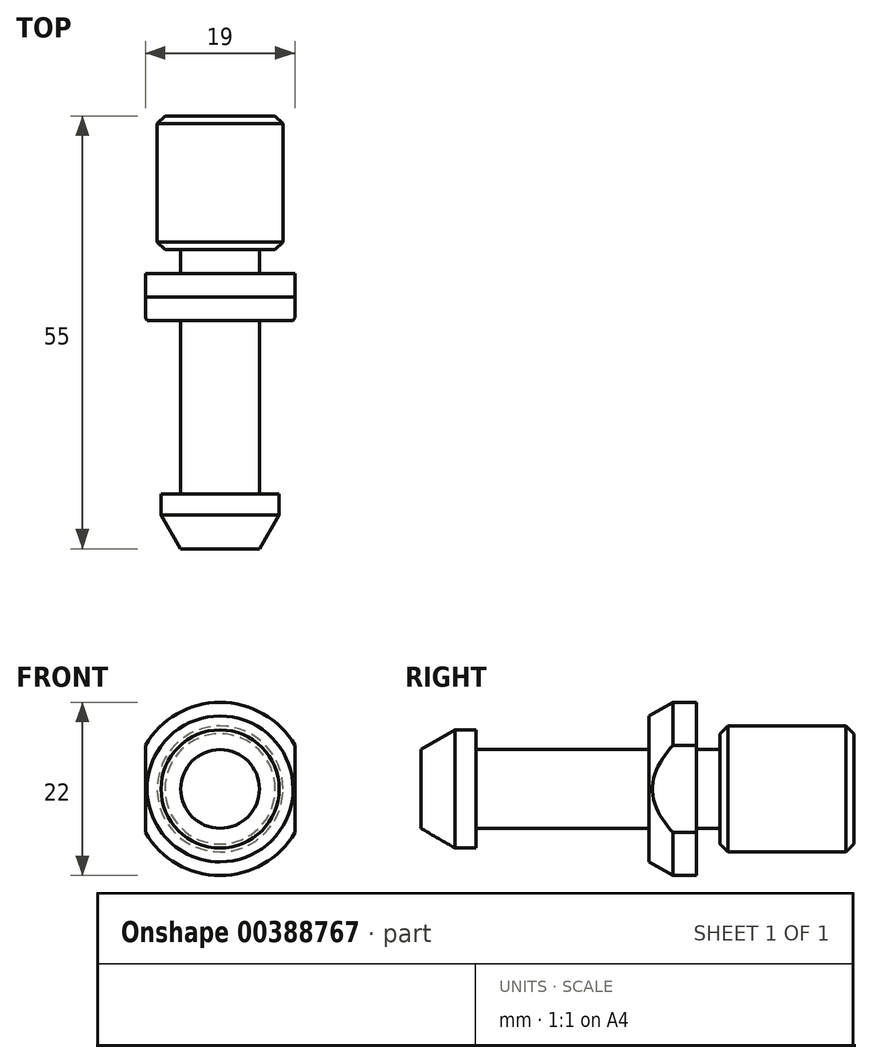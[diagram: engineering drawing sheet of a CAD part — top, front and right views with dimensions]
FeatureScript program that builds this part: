
annotation { "Feature Type Name" : "Feature", "Feature Type Description" : "" }
export const myFeature = defineFeature(function(context is Context, id is Id, definition is map)
    precondition{}
    {
        {
            var Q0;
            Q0=qCreatedBy(makeId("Right.planeOp"),FACE);
            var sketch = newSketch(context, id + "F0", { "sketchPlane" : qUnion([Q0])});
            skLineSegment(sketch, "E0", {"start": v(-37.86, 0) * mm, "end": v(38.7, 0) * mm, "construction": true});
            skLineSegment(sketch, "E1.bottom", {"start": v(0, 0) * mm, "end": v(-22, 0) * mm});
            skLineSegment(sketch, "E1.top", {"start": v(0, 5) * mm, "end": v(-22, 5) * mm});
            skLineSegment(sketch, "E1.left", {"start": v(0, 0) * mm, "end": v(0, 5) * mm});
            skLineSegment(sketch, "E1.right", {"start": v(-22, 0) * mm, "end": v(-22, 5) * mm});
            skLineSegment(sketch, "E2.bottom", {"start": v(-22, 0) * mm, "end": v(-24.67, 0) * mm});
            skLineSegment(sketch, "E2.top", {"start": v(-22, 7.5) * mm, "end": v(-24.67, 7.5) * mm});
            skLineSegment(sketch, "E2.left", {"start": v(-22, 0) * mm, "end": v(-22, 7.5) * mm});
            skLineSegment(sketch, "E2.right", {"start": v(-24.67, 0) * mm, "end": v(-24.67, 7.5) * mm});
            skLineSegment(sketch, "E3", {"start": v(-24.67, 7.5) * mm, "end": v(-29, 5) * mm});
            skLineSegment(sketch, "E4", {"start": v(-29, 5) * mm, "end": v(-29, 0) * mm});
            skLineSegment(sketch, "E5", {"start": v(-29, 5) * mm, "end": v(-22, 5) * mm, "construction": true});
            skLineSegment(sketch, "E6.bottom", {"start": v(0, 0) * mm, "end": v(6, 0) * mm, "construction": true});
            skLineSegment(sketch, "E6.top", {"start": v(0, 11) * mm, "end": v(6, 11) * mm, "construction": true});
            skLineSegment(sketch, "E6.left", {"start": v(0, 0) * mm, "end": v(0, 11) * mm, "construction": true});
            skLineSegment(sketch, "E6.right", {"start": v(6, 0) * mm, "end": v(6, 11) * mm, "construction": true});
            skLineSegment(sketch, "E7.bottom", {"start": v(6, 0) * mm, "end": v(3, 0) * mm});
            skLineSegment(sketch, "E7.top", {"start": v(6, 11) * mm, "end": v(3, 11) * mm});
            skLineSegment(sketch, "E7.left", {"start": v(6, 0) * mm, "end": v(6, 11) * mm});
            skLineSegment(sketch, "E7.right", {"start": v(3, 0) * mm, "end": v(3, 11) * mm});
            skLineSegment(sketch, "E8", {"start": v(3, 11) * mm, "end": v(0, 9.27) * mm});
            skLineSegment(sketch, "E9", {"start": v(0, 9.27) * mm, "end": v(0, 0) * mm});
            skLineSegment(sketch, "E10", {"start": v(0, 0) * mm, "end": v(6, 0) * mm});
            skLineSegment(sketch, "E11", {"start": v(-29, 0) * mm, "end": v(-24.67, 0) * mm});
            skLineSegment(sketch, "E12.bottom", {"start": v(6, 0) * mm, "end": v(9, 0) * mm});
            skLineSegment(sketch, "E12.top", {"start": v(6, 5) * mm, "end": v(9, 5) * mm});
            skLineSegment(sketch, "E12.left", {"start": v(6, 0) * mm, "end": v(6, 5) * mm});
            skLineSegment(sketch, "E12.right", {"start": v(9, 0) * mm, "end": v(9, 5) * mm});
            skLineSegment(sketch, "E13.bottom", {"start": v(9, 0) * mm, "end": v(26, 0) * mm});
            skLineSegment(sketch, "E13.top", {"start": v(9, 8) * mm, "end": v(26, 8) * mm});
            skLineSegment(sketch, "E13.left", {"start": v(9, 0) * mm, "end": v(9, 8) * mm});
            skLineSegment(sketch, "E13.right", {"start": v(26, 0) * mm, "end": v(26, 8) * mm});
            skSolve(sketch);
        }
        {
            var Q0;
            Q0 = qSketchRegion(id + "F0", true);
            var Q1;
            Q1=sQuery(id+"F0.wireOp",EDGE,"E0");
            revolve(context, id + "F1", {"entities" : qUnion([Q0]), "axis" : qUnion([Q1]), "revolveType" : RevolveType.FULL});
        }
        {
            var Q0;
            Q0=makeQuery(id+"F1.opRevolve","SWEPT_EDGE",EDGE,{"disambiguationData":[OSD([sQuery(id+"F0.wireOp",EDGE,"E13.top"),sQuery(id+"F0.wireOp",EDGE,"E13.left")])]});
            var Q1;
            Q1=makeQuery(id+"F1.opRevolve","SWEPT_EDGE",EDGE,{"disambiguationData":[OSD([sQuery(id+"F0.wireOp",EDGE,"E13.top"),sQuery(id+"F0.wireOp",EDGE,"E13.right")])]});
            chamfer(context, id + "F2", {"entities" : qUnion([Q0, Q1]), "width" : 1 * mm, "tangentPropagation" : true});
        }
        {
            var Q0;
            Q0=qCreatedBy(makeId("Front.planeOp"),FACE);
            var sketch = newSketch(context, id + "F3", { "sketchPlane" : qUnion([Q0])});
            skCircle(sketch, "E14", {"center": v(0, 0) * mm, "radius": 11 * mm, "construction": true});
            skLineSegment(sketch, "E15", {"start": v(0, -11) * mm, "end": v(0, 11) * mm, "construction": true});
            skLineSegment(sketch, "E16", {"start": v(0, 11) * mm, "end": v(0, 0) * mm, "construction": true});
            skLineSegment(sketch, "E17", {"start": v(-11, 0) * mm, "end": v(11, 0) * mm, "construction": true});
            skLineSegment(sketch, "E18.bottom", {"start": v(-9.5, -5.55) * mm, "end": v(9.5, -5.55) * mm, "construction": true});
            skLineSegment(sketch, "E18.top", {"start": v(-9.5, 5.55) * mm, "end": v(9.5, 5.55) * mm, "construction": true});
            skLineSegment(sketch, "E18.left", {"start": v(-9.5, -5.55) * mm, "end": v(-9.5, 5.55) * mm, "construction": true});
            skLineSegment(sketch, "E18.right", {"start": v(9.5, -5.55) * mm, "end": v(9.5, 5.55) * mm, "construction": true});
            skLineSegment(sketch, "E19.bottom", {"start": v(9.5, -5.55) * mm, "end": v(12.5, -5.55) * mm});
            skLineSegment(sketch, "E19.top", {"start": v(9.5, 5.55) * mm, "end": v(12.5, 5.55) * mm});
            skLineSegment(sketch, "E19.left", {"start": v(9.5, -5.55) * mm, "end": v(9.5, 5.55) * mm});
            skLineSegment(sketch, "E19.right", {"start": v(12.5, -5.55) * mm, "end": v(12.5, 5.55) * mm});
            skLineSegment(sketch, "E20.bottom", {"start": v(-9.5, -5.55) * mm, "end": v(-12.5, -5.55) * mm});
            skLineSegment(sketch, "E20.top", {"start": v(-9.5, 5.55) * mm, "end": v(-12.5, 5.55) * mm});
            skLineSegment(sketch, "E20.left", {"start": v(-9.5, -5.55) * mm, "end": v(-9.5, 5.55) * mm});
            skLineSegment(sketch, "E20.right", {"start": v(-12.5, -5.55) * mm, "end": v(-12.5, 5.55) * mm});
            skSolve(sketch);
        }
        {
            var Q0;
            Q0 = qSketchRegion(id + "F3", true);
            extrude(context, id + "F4", {"entities" : qUnion([Q0]), "operationType" : NewBodyOperationType.REMOVE, "oppositeDirection" : true, "depth" : 27.26 * mm});
        }
    });
